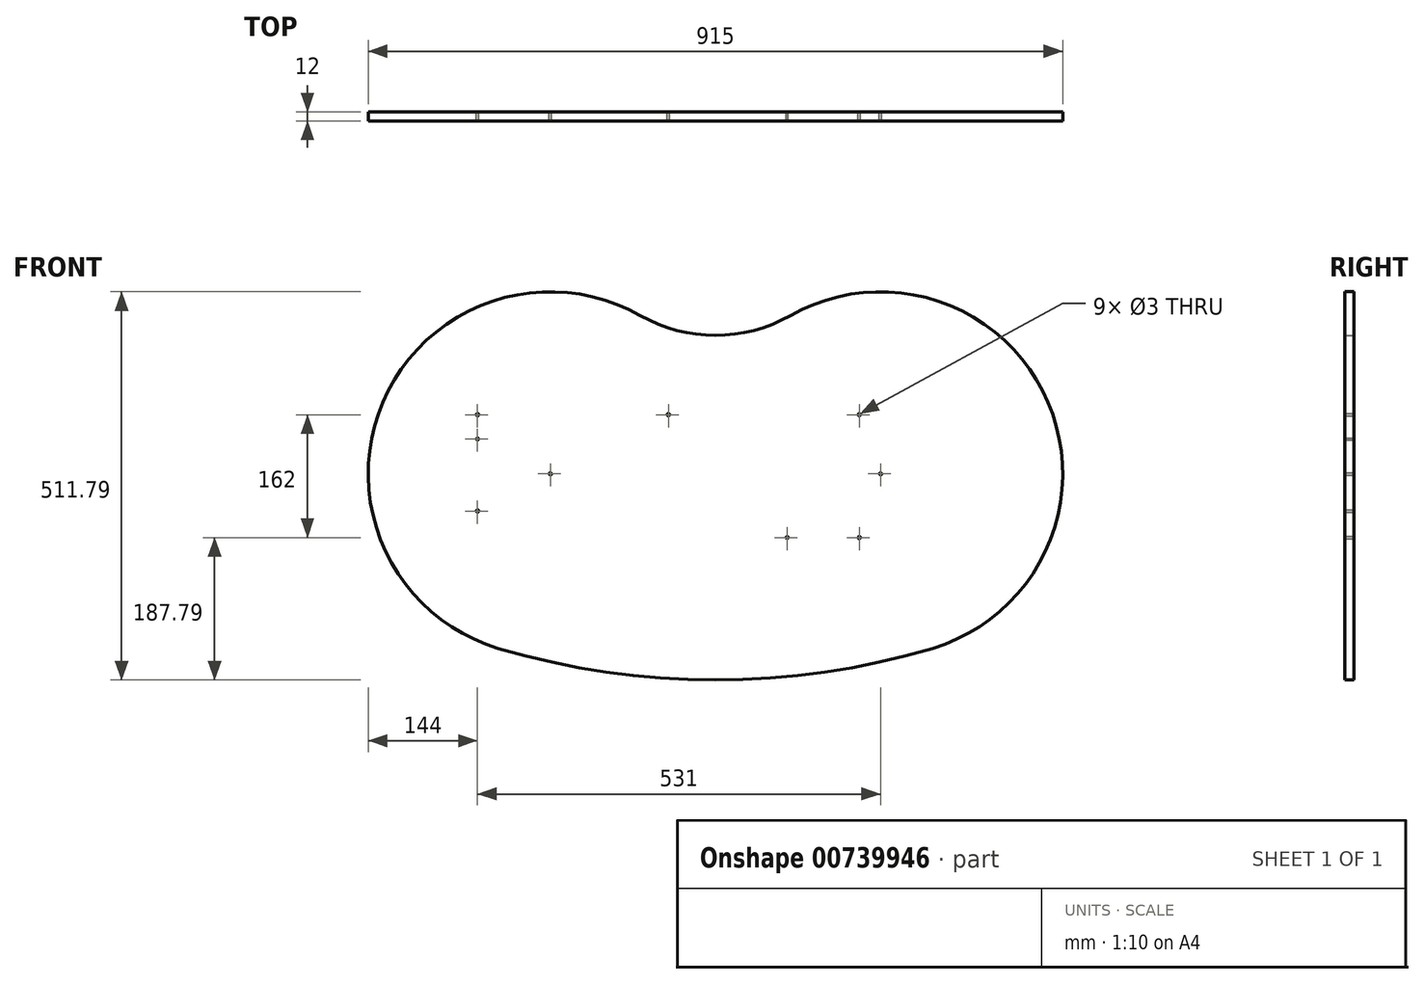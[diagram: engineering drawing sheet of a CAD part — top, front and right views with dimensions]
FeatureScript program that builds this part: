
annotation { "Feature Type Name" : "Feature", "Feature Type Description" : "" }
export const myFeature = defineFeature(function(context is Context, id is Id, definition is map)
    precondition{}
    {
        {
            var Q0;
            Q0=qCreatedBy(makeId("Front.planeOp"),FACE);
            var sketch = newSketch(context, id + "F0", { "sketchPlane" : qUnion([Q0])});
            skArc(sketch, "E0.MirrorCS", {"start": v(-286.18, -229.96) * mm, "mid": v(-438.21, 94.27) * mm, "end": v(-98.86, 208.63) * mm});
            skArc(sketch, "E1.MirrorCS", {"start": v(98.86, 208.63) * mm, "mid": v(438.21, 94.27) * mm, "end": v(286.18, -229.96) * mm});
            skArc(sketch, "E2.MirrorCS", {"start": v(286.18, -229.96) * mm, "mid": v(0, -271.79) * mm, "end": v(-286.18, -229.96) * mm});
            skArc(sketch, "E3.MirrorCS", {"start": v(98.86, 208.63) * mm, "mid": v(0, 182.48) * mm, "end": v(-98.86, 208.63) * mm});
            skCircle(sketch, "E4", {"center": v(189.5, -84) * mm, "radius": 1.5 * mm});
            skCircle(sketch, "E5", {"center": v(94.5, -84) * mm, "radius": 1.5 * mm});
            skLineSegment(sketch, "E6.bottom", {"start": v(205.5, -68) * mm, "end": v(78.5, -68) * mm, "construction": true});
            skLineSegment(sketch, "E6.top", {"start": v(205.5, -100) * mm, "end": v(78.5, -100) * mm, "construction": true});
            skLineSegment(sketch, "E6.left", {"start": v(205.5, -68) * mm, "end": v(205.5, -100) * mm, "construction": true});
            skLineSegment(sketch, "E6.right", {"start": v(78.5, -68) * mm, "end": v(78.5, -100) * mm, "construction": true});
            skLineSegment(sketch, "E7.bottom", {"start": v(205.5, -100) * mm, "end": v(217.5, -100) * mm, "construction": true});
            skLineSegment(sketch, "E7.top", {"start": v(205.5, 154) * mm, "end": v(217.5, 154) * mm, "construction": true});
            skLineSegment(sketch, "E7.left", {"start": v(205.5, -100) * mm, "end": v(205.5, 154) * mm, "construction": true});
            skLineSegment(sketch, "E7.right", {"start": v(217.5, -100) * mm, "end": v(217.5, 154) * mm, "construction": true});
            skLineSegment(sketch, "E8.bottom", {"start": v(205.5, 94) * mm, "end": v(-329.5, 94) * mm, "construction": true});
            skLineSegment(sketch, "E8.top", {"start": v(205.5, 62) * mm, "end": v(-329.5, 62) * mm, "construction": true});
            skLineSegment(sketch, "E8.left", {"start": v(205.5, 94) * mm, "end": v(205.5, 62) * mm, "construction": true});
            skLineSegment(sketch, "E8.right", {"start": v(-329.5, 94) * mm, "end": v(-329.5, 62) * mm, "construction": true});
            skLineSegment(sketch, "E9.bottom", {"start": v(-329.5, 62) * mm, "end": v(-297.5, 62) * mm, "construction": true});
            skLineSegment(sketch, "E9.top", {"start": v(-329.5, -65) * mm, "end": v(-297.5, -65) * mm, "construction": true});
            skLineSegment(sketch, "E9.left", {"start": v(-329.5, 62) * mm, "end": v(-329.5, -65) * mm, "construction": true});
            skLineSegment(sketch, "E9.right", {"start": v(-297.5, 62) * mm, "end": v(-297.5, -65) * mm, "construction": true});
            skCircle(sketch, "E10", {"center": v(189.5, 78) * mm, "radius": 1.5 * mm});
            skCircle(sketch, "E11", {"center": v(-313.5, 78) * mm, "radius": 1.5 * mm});
            skCircle(sketch, "E12", {"center": v(-313.5, 46) * mm, "radius": 1.5 * mm});
            skCircle(sketch, "E13", {"center": v(-313.5, -49) * mm, "radius": 1.5 * mm});
            skCircle(sketch, "E14", {"center": v(-62, 78) * mm, "radius": 1.5 * mm});
            skCircle(sketch, "E15", {"center": v(-217.5, 0) * mm, "radius": 1.5 * mm});
            skCircle(sketch, "E16", {"center": v(217.5, 0) * mm, "radius": 1.5 * mm});
            skSolve(sketch);
        }
        {
            var Q0;
            Q0 = qSketchRegion(id + "F0", true);
            extrude(context, id + "F1", {"entities" : qUnion([Q0]), "depth" : 12 * mm, "offsetDistance" : 25 * mm, "symmetric" : true});
        }
    });
